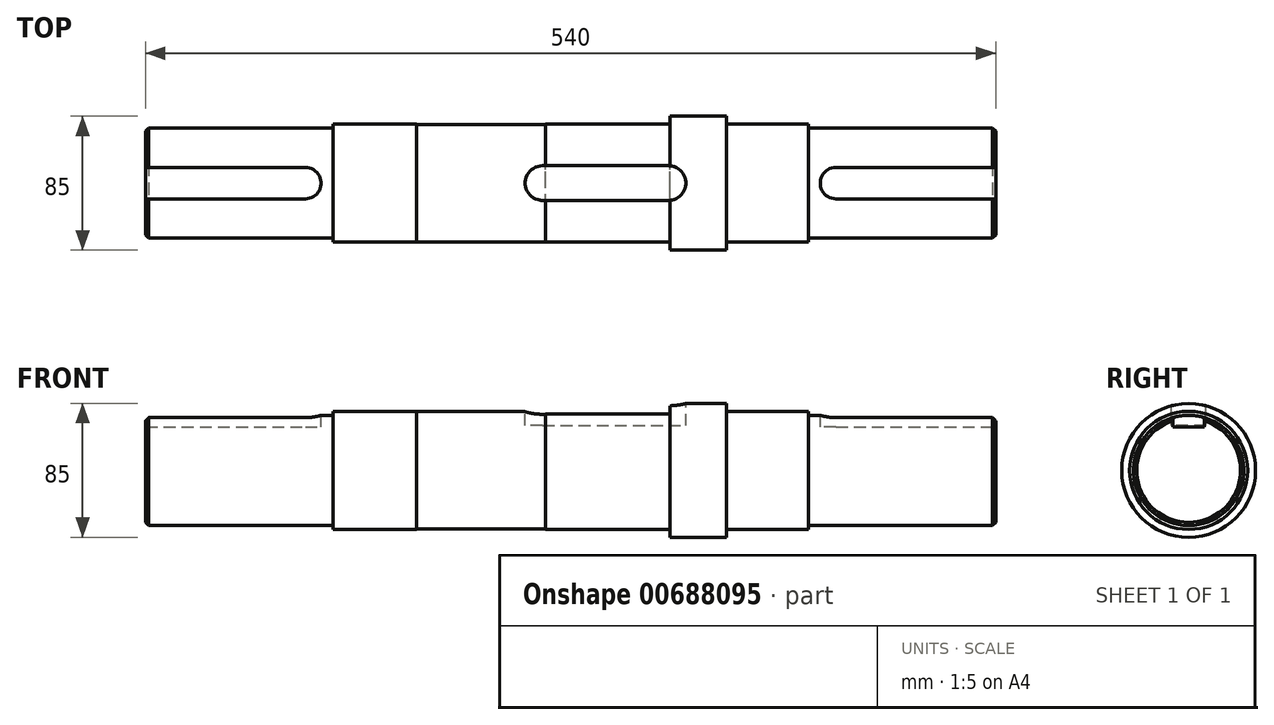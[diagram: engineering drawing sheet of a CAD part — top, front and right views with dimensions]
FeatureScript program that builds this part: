
annotation { "Feature Type Name" : "Feature", "Feature Type Description" : "" }
export const myFeature = defineFeature(function(context is Context, id is Id, definition is map)
    precondition{}
    {
        {
            var Q0;
            Q0=qCreatedBy(makeId("Front.planeOp"),FACE);
            var sketch = newSketch(context, id + "F0", { "sketchPlane" : qUnion([Q0])});
            skLineSegment(sketch, "E0", {"start": v(-291, 0) * mm, "end": v(-291, 35) * mm});
            skLineSegment(sketch, "E1", {"start": v(-291, 35) * mm, "end": v(-151, 35) * mm});
            skLineSegment(sketch, "E2", {"start": v(-151, 35) * mm, "end": v(-151, 37.5) * mm});
            skLineSegment(sketch, "E3", {"start": v(-151, 37.5) * mm, "end": v(-98, 37.5) * mm});
            skLineSegment(sketch, "E4", {"start": v(-98, 37.3) * mm, "end": v(-98, 37.5) * mm});
            skLineSegment(sketch, "E5", {"start": v(-98, 37.3) * mm, "end": v(-16, 37.3) * mm});
            skLineSegment(sketch, "E6", {"start": v(-16, 37.5) * mm, "end": v(-16, 37.3) * mm});
            skLineSegment(sketch, "E7", {"start": v(-16, 37.5) * mm, "end": v(63, 37.5) * mm});
            skLineSegment(sketch, "E8", {"start": v(63, 42.5) * mm, "end": v(63, 37.5) * mm});
            skLineSegment(sketch, "E9", {"start": v(63, 42.5) * mm, "end": v(99, 42.5) * mm});
            skLineSegment(sketch, "E10", {"start": v(99, 37.5) * mm, "end": v(99, 42.5) * mm});
            skLineSegment(sketch, "E11", {"start": v(99, 37.5) * mm, "end": v(151, 37.5) * mm});
            skLineSegment(sketch, "E12", {"start": v(151, 37.5) * mm, "end": v(151, 35) * mm});
            skLineSegment(sketch, "E13", {"start": v(151, 35) * mm, "end": v(291, 35) * mm});
            skLineSegment(sketch, "E14", {"start": v(291, 35) * mm, "end": v(291, 0) * mm});
            skLineSegment(sketch, "E15", {"start": v(291, 0) * mm, "end": v(-291, 0) * mm});
            skLineSegment(sketch, "E16", {"start": v(-291, 35) * mm, "end": v(-291, -35) * mm, "construction": true});
            skLineSegment(sketch, "E17", {"start": v(291, 35) * mm, "end": v(291, -35) * mm, "construction": true});
            skSolve(sketch);
        }
        {
            var Q0;
            Q0=makeQuery(id+"F0.imprint","IMPRINT",FACE,{"disambiguationData":[TD([[makeQuery(id+"F0.imprint","IMPRINT",EDGE,{"derivedFrom":sQuery(id+"F0.wireOp",EDGE,"E0")}),-1.0]])]});
            var Q1;
            Q1=sQuery(id+"F0.wireOp",EDGE,"E15");
            revolve(context, id + "F1", {"entities" : qUnion([Q0]), "axis" : qUnion([Q1]), "revolveType" : RevolveType.FULL});
        }
        {
            var Q0;
            Q0=qCreatedBy(makeId("Top.planeOp"),FACE);
            cPlane(context, id + "F2", {"entities" : qUnion([Q0]), "cplaneType" : CPlaneType.OFFSET, "offset" : 35 * mm, "width" : 150 * mm, "height" : 150 * mm});
        }
        {
            var Q0;
            Q0=qCreatedBy(id+"F2.planeOp",FACE);
            var sketch = newSketch(context, id + "F3", { "sketchPlane" : qUnion([Q0])});
            skLineSegment(sketch, "E18.bottom", {"start": v(-273.5, 10) * mm, "end": v(-168.5, 10) * mm});
            skLineSegment(sketch, "E18.top", {"start": v(-273.5, -10) * mm, "end": v(-168.5, -10) * mm});
            skLineSegment(sketch, "E18.left", {"start": v(-273.5, 10) * mm, "end": v(-273.5, -10) * mm});
            skLineSegment(sketch, "E18.right", {"start": v(-168.5, 10) * mm, "end": v(-168.5, -10) * mm});
            skPoint(sketch, "E18.middle", {"position": v(-221, 0) * mm});
            skLineSegment(sketch, "E19.bottom", {"start": v(168.5, 10) * mm, "end": v(273.5, 10) * mm});
            skLineSegment(sketch, "E19.top", {"start": v(168.5, -10) * mm, "end": v(273.5, -10) * mm});
            skLineSegment(sketch, "E19.left", {"start": v(168.5, 10) * mm, "end": v(168.5, -10) * mm});
            skLineSegment(sketch, "E19.right", {"start": v(273.5, 10) * mm, "end": v(273.5, -10) * mm});
            skPoint(sketch, "E19.middle", {"position": v(221, 0) * mm});
            skCircle(sketch, "E20", {"center": v(-273.5, 0) * mm, "radius": 10 * mm});
            skCircle(sketch, "E21", {"center": v(-168.5, 0) * mm, "radius": 10 * mm});
            skCircle(sketch, "E22", {"center": v(168.5, 0) * mm, "radius": 10 * mm});
            skCircle(sketch, "E23", {"center": v(273.5, 0) * mm, "radius": 10 * mm});
            skSolve(sketch);
        }
        {
            var Q0;
            {var subQ0=sQuery(id+"F3.wireOp",EDGE,"E18.bottom");Q0=makeQuery(id+"F3.imprint","IMPRINT",FACE,{"disambiguationData":[TD([[makeQuery(id+"F3.imprint","IMPRINT",EDGE,{"derivedFrom":subQ0}),-1.0]])]});}
            var Q1;
            {var subQ0=sQuery(id+"F3.wireOp",EDGE,"E18.left");Q1=makeQuery(id+"F3.imprint","IMPRINT",FACE,{"disambiguationData":[TD([[makeQuery(id+"F3.imprint","IMPRINT",EDGE,{"derivedFrom":subQ0}),1.0]])]});}
            var Q2;
            {var subQ0=sQuery(id+"F3.wireOp",EDGE,"E18.left");Q2=makeQuery(id+"F3.imprint","IMPRINT",FACE,{"disambiguationData":[TD([[makeQuery(id+"F3.imprint","IMPRINT",EDGE,{"derivedFrom":subQ0}),-1.0]])]});}
            var Q3;
            {var subQ0=sQuery(id+"F3.wireOp",EDGE,"E18.right");Q3=makeQuery(id+"F3.imprint","IMPRINT",FACE,{"disambiguationData":[TD([[makeQuery(id+"F3.imprint","IMPRINT",EDGE,{"derivedFrom":subQ0}),-1.0]])]});}
            var Q4;
            {var subQ0=sQuery(id+"F3.wireOp",EDGE,"E18.right");Q4=makeQuery(id+"F3.imprint","IMPRINT",FACE,{"disambiguationData":[TD([[makeQuery(id+"F3.imprint","IMPRINT",EDGE,{"derivedFrom":subQ0}),1.0]])]});}
            var Q5;
            {var subQ0=sQuery(id+"F3.wireOp",EDGE,"E19.left");Q5=makeQuery(id+"F3.imprint","IMPRINT",FACE,{"disambiguationData":[TD([[makeQuery(id+"F3.imprint","IMPRINT",EDGE,{"derivedFrom":subQ0}),-1.0]])]});}
            var Q6;
            {var subQ0=sQuery(id+"F3.wireOp",EDGE,"E19.left");Q6=makeQuery(id+"F3.imprint","IMPRINT",FACE,{"disambiguationData":[TD([[makeQuery(id+"F3.imprint","IMPRINT",EDGE,{"derivedFrom":subQ0}),1.0]])]});}
            var Q7;
            {var subQ0=sQuery(id+"F3.wireOp",EDGE,"E19.right");Q7=makeQuery(id+"F3.imprint","IMPRINT",FACE,{"disambiguationData":[TD([[makeQuery(id+"F3.imprint","IMPRINT",EDGE,{"derivedFrom":subQ0}),-1.0]])]});}
            var Q8;
            {var subQ0=sQuery(id+"F3.wireOp",EDGE,"E19.right");Q8=makeQuery(id+"F3.imprint","IMPRINT",FACE,{"disambiguationData":[TD([[makeQuery(id+"F3.imprint","IMPRINT",EDGE,{"derivedFrom":subQ0}),1.0]])]});}
            var Q9;
            {var subQ0=sQuery(id+"F3.wireOp",EDGE,"E19.bottom");Q9=makeQuery(id+"F3.imprint","IMPRINT",FACE,{"disambiguationData":[TD([[makeQuery(id+"F3.imprint","IMPRINT",EDGE,{"derivedFrom":subQ0}),-1.0]])]});}
            extrude(context, id + "F4", {"entities" : qUnion([Q0, Q1, Q2, Q3, Q4, Q5, Q6, Q7, Q8, Q9]), "operationType" : NewBodyOperationType.REMOVE, "oppositeDirection" : true, "depth" : 7.5 * mm, "offsetDistance" : 25 * mm});
        }
        {
            var Q0;
            Q0=qCreatedBy(makeId("Top.planeOp"),FACE);
            cPlane(context, id + "F5", {"entities" : qUnion([Q0]), "cplaneType" : CPlaneType.OFFSET, "offset" : 37.5 * mm, "width" : 150 * mm, "height" : 150 * mm});
        }
        {
            var Q0;
            Q0=qCreatedBy(id+"F5.planeOp",FACE);
            var sketch = newSketch(context, id + "F6", { "sketchPlane" : qUnion([Q0])});
            skLineSegment(sketch, "E24.bottom", {"start": v(-17.9, 11) * mm, "end": v(62.1, 11) * mm});
            skLineSegment(sketch, "E24.top", {"start": v(-17.9, -11) * mm, "end": v(62.1, -11) * mm});
            skLineSegment(sketch, "E24.left", {"start": v(62.1, 11) * mm, "end": v(62.1, -11) * mm});
            skLineSegment(sketch, "E24.right", {"start": v(-17.9, 11) * mm, "end": v(-17.9, -11) * mm});
            skPoint(sketch, "E24.middle", {"position": v(22.1, 0) * mm});
            skCircle(sketch, "E25", {"center": v(62.1, 0) * mm, "radius": 11 * mm});
            skCircle(sketch, "E26", {"center": v(-17.9, 0) * mm, "radius": 11 * mm});
            skSolve(sketch);
        }
        {
            var Q0;
            {var subQ0=sQuery(id+"F6.wireOp",EDGE,"E24.left");Q0=makeQuery(id+"F6.imprint","IMPRINT",FACE,{"disambiguationData":[TD([[makeQuery(id+"F6.imprint","IMPRINT",EDGE,{"derivedFrom":subQ0}),1.0]])]});}
            var Q1;
            {var subQ0=sQuery(id+"F6.wireOp",EDGE,"E24.bottom");Q1=makeQuery(id+"F6.imprint","IMPRINT",FACE,{"disambiguationData":[TD([[makeQuery(id+"F6.imprint","IMPRINT",EDGE,{"derivedFrom":subQ0}),-1.0]])]});}
            var Q2;
            {var subQ0=sQuery(id+"F6.wireOp",EDGE,"E24.left");Q2=makeQuery(id+"F6.imprint","IMPRINT",FACE,{"disambiguationData":[TD([[makeQuery(id+"F6.imprint","IMPRINT",EDGE,{"derivedFrom":subQ0}),-1.0]])]});}
            var Q3;
            {var subQ0=sQuery(id+"F6.wireOp",EDGE,"E24.right");Q3=makeQuery(id+"F6.imprint","IMPRINT",FACE,{"disambiguationData":[TD([[makeQuery(id+"F6.imprint","IMPRINT",EDGE,{"derivedFrom":subQ0}),-1.0]])]});}
            var Q4;
            {var subQ0=sQuery(id+"F6.wireOp",EDGE,"E24.right");Q4=makeQuery(id+"F6.imprint","IMPRINT",FACE,{"disambiguationData":[TD([[makeQuery(id+"F6.imprint","IMPRINT",EDGE,{"derivedFrom":subQ0}),1.0]])]});}
            extrude(context, id + "F7", {"entities" : qUnion([Q0, Q1, Q2, Q3, Q4]), "operationType" : NewBodyOperationType.REMOVE, "oppositeDirection" : true, "depth" : 9 * mm, "offsetDistance" : 25 * mm});
        }
        {
            var Q0;
            Q0=makeQuery(id+"F7.boolean.opBoolean","COPY",FACE,{"derivedFrom":makeQuery(id+"F7.opExtrude","CAP_FACE",FACE,{"disambiguationData":[OSD([sQuery(id+"F6.wireOp",EDGE,"E24.bottom"),sQuery(id+"F6.wireOp",EDGE,"E24.top"),sQuery(id+"F6.wireOp",EDGE,"E25"),sQuery(id+"F6.wireOp",EDGE,"E26")])],"isStart":false})});
            extrude(context, id + "F8", {"entities" : qUnion([Q0]), "operationType" : NewBodyOperationType.REMOVE, "endBound" : BoundingType.THROUGH_ALL, "depth" : 25 * mm, "offsetDistance" : 25 * mm});
        }
        {
            var Q0;
            Q0=qCreatedBy(makeId("Top.planeOp"),FACE);
            var sketch = newSketch(context, id + "F9", { "sketchPlane" : qUnion([Q0])});
            skLineSegment(sketch, "E27.bottom", {"start": v(-331.8, 54.4) * mm, "end": v(-270, 54.4) * mm});
            skLineSegment(sketch, "E27.top", {"start": v(-331.8, -54.4) * mm, "end": v(-270, -54.4) * mm});
            skLineSegment(sketch, "E27.left", {"start": v(-331.8, 54.4) * mm, "end": v(-331.8, -54.4) * mm});
            skLineSegment(sketch, "E27.right", {"start": v(-270, 54.4) * mm, "end": v(-270, -54.4) * mm});
            skPoint(sketch, "E27.middle", {"position": v(-300.9, 0) * mm});
            skLineSegment(sketch, "E28.bottom", {"start": v(322.8, 69.57) * mm, "end": v(270, 69.57) * mm});
            skLineSegment(sketch, "E28.top", {"start": v(322.8, -69.57) * mm, "end": v(270, -69.57) * mm});
            skLineSegment(sketch, "E28.left", {"start": v(322.8, 69.57) * mm, "end": v(322.8, -69.57) * mm});
            skLineSegment(sketch, "E28.right", {"start": v(270, 69.57) * mm, "end": v(270, -69.57) * mm});
            skPoint(sketch, "E28.middle", {"position": v(296.4, 0) * mm});
            skLineSegment(sketch, "E29", {"start": v(-270, 0) * mm, "end": v(270, 0) * mm, "construction": true});
            skSolve(sketch);
        }
        {
            var Q0;
            Q0=makeQuery(id+"F9.imprint","IMPRINT",FACE,{"disambiguationData":[TD([[makeQuery(id+"F9.imprint","IMPRINT",EDGE,{"derivedFrom":sQuery(id+"F9.wireOp",EDGE,"E27.bottom")}),-1.0]])]});
            var Q1;
            Q1=makeQuery(id+"F9.imprint","IMPRINT",FACE,{"disambiguationData":[TD([[makeQuery(id+"F9.imprint","IMPRINT",EDGE,{"derivedFrom":sQuery(id+"F9.wireOp",EDGE,"E28.bottom")}),1.0]])]});
            extrude(context, id + "F10", {"entities" : qUnion([Q0, Q1]), "operationType" : NewBodyOperationType.REMOVE, "endBound" : BoundingType.THROUGH_ALL, "oppositeDirection" : true, "depth" : 25 * mm, "offsetDistance" : 25 * mm});
        }
        {
            var Q0;
            Q0=makeQuery(id+"F10.boolean.opBoolean","COPY",FACE,{"derivedFrom":makeQuery(id+"F10.opExtrude","CAP_FACE",FACE,{"disambiguationData":[OSD([sQuery(id+"F9.wireOp",EDGE,"E27.bottom"),sQuery(id+"F9.wireOp",EDGE,"E27.top"),sQuery(id+"F9.wireOp",EDGE,"E27.left"),sQuery(id+"F9.wireOp",EDGE,"E27.right")])],"isStart":true})});
            var Q1;
            Q1=makeQuery(id+"F10.boolean.opBoolean","COPY",FACE,{"derivedFrom":makeQuery(id+"F10.opExtrude","CAP_FACE",FACE,{"disambiguationData":[OSD([sQuery(id+"F9.wireOp",EDGE,"E28.bottom"),sQuery(id+"F9.wireOp",EDGE,"E28.top"),sQuery(id+"F9.wireOp",EDGE,"E28.left"),sQuery(id+"F9.wireOp",EDGE,"E28.right")])],"isStart":true})});
            extrude(context, id + "F11", {"entities" : qUnion([Q0, Q1]), "operationType" : NewBodyOperationType.REMOVE, "endBound" : BoundingType.THROUGH_ALL, "oppositeDirection" : true, "depth" : 25 * mm, "offsetDistance" : 25 * mm});
        }
        {
            var Q0;
            Q0=makeQuery(id+"F11.boolean.opBoolean","INTERSECT",EDGE,{"derivedFrom":[makeQuery(id+"F1.opRevolve","SWEPT_FACE",FACE,{"disambiguationData":[OSD([sQuery(id+"F0.wireOp",EDGE,"E1")])]}),makeQuery(id+"F11.opExtrude","SWEPT_FACE",FACE,{"disambiguationData":[OSD([sQuery(id+"F9.wireOp",EDGE,"E27.right")])]})]});
            var Q1;
            Q1=makeQuery(id+"F11.boolean.opBoolean","INTERSECT",EDGE,{"derivedFrom":[makeQuery(id+"F1.opRevolve","SWEPT_FACE",FACE,{"disambiguationData":[OSD([sQuery(id+"F0.wireOp",EDGE,"E13")])]}),makeQuery(id+"F11.opExtrude","SWEPT_FACE",FACE,{"disambiguationData":[OSD([sQuery(id+"F9.wireOp",EDGE,"E28.right")])]})]});
            chamfer(context, id + "F12", {"entities" : qUnion([Q0, Q1]), "width" : 2 * mm, "tangentPropagation" : true});
        }
    });
